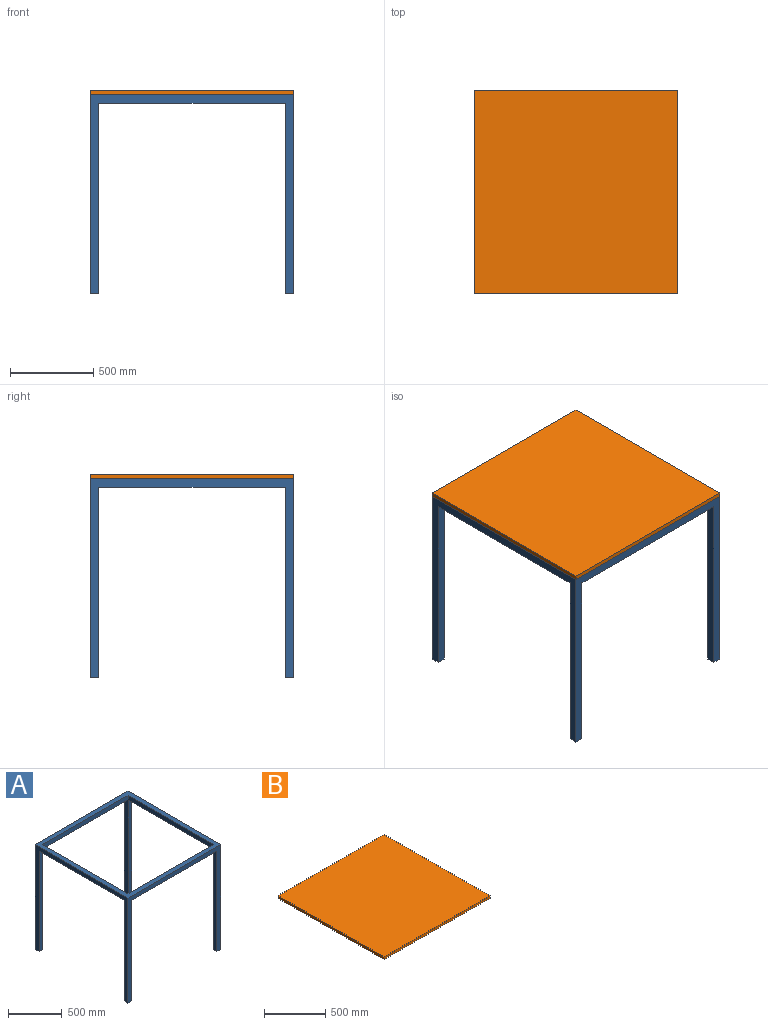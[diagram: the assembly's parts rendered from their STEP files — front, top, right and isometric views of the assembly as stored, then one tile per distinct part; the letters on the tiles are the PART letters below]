
ASSEMBLY  parts=2 mates=1
PART A: 25 faces, bbox 1219.2x1219.2x1193.8 mm
  f0: plane 1117.6x50.8mm, normal (0,0,-1), area 56774.1mm2, adj f6,f10,f20,f22
  f1: plane 1117.6x50.8mm, normal (0,0,-1), area 56774.1mm2, adj f8,f9,f17,f19
  f2: plane 1117.6x50.8mm, normal (0,0,-1), area 56774.1mm2, adj f5,f12,f14,f16
  f3: plane 1117.6x50.8mm, normal (0,0,-1), area 56774.1mm2, adj f7,f11,f13,f23
  f4: plane 1219.2x1219.2mm, normal (0,0,1), area 237418.9mm2, adj f5,f6,f7,f8,f9,f10,f11,f12
  f5: plane 1219.2x1193.8mm, normal (0,1,0), area 178064.2mm2, adj f2,f4,f7,f8,f14,f15,f16,f18
  f6: plane 1219.2x1193.8mm, normal (0,-1,0), area 178064.2mm2, adj f0,f4,f7,f8,f20,f21,f22,f24
  f7: plane 1219.2x1193.8mm, normal (1,0,0), area 178064.2mm2, adj f3,f4,f5,f6,f13,f15,f23,f24
  f8: plane 1219.2x1193.8mm, normal (-1,0,0), area 178064.2mm2, adj f1,f4,f5,f6,f17,f18,f19,f21
  f9: plane 1117.6x50.8mm, normal (1,0,0), area 56774.1mm2, adj f1,f4,f10,f12
  f10: plane 1117.6x50.8mm, normal (0,1,0), area 56774.1mm2, adj f0,f4,f9,f11
  f11: plane 1117.6x50.8mm, normal (-1,0,0), area 56774.1mm2, adj f3,f4,f10,f12
  f12: plane 1117.6x50.8mm, normal (0,-1,0), area 56774.1mm2, adj f2,f4,f9,f11
  f13: plane 1143x50.8mm, normal (0,-1,0), area 58064.4mm2, adj f3,f7,f14,f15
  f14: plane 1143x50.8mm, normal (-1,0,0), area 58064.4mm2, adj f2,f5,f13,f15
  f15: plane 50.8x50.8mm, normal (0,0,-1), area 2580.6mm2, adj f5,f7,f13,f14
  f16: plane 1143x50.8mm, normal (1,0,0), area 58064.4mm2, adj f2,f5,f17,f18
  f17: plane 1143x50.8mm, normal (0,-1,0), area 58064.4mm2, adj f1,f8,f16,f18
  f18: plane 50.8x50.8mm, normal (0,0,-1), area 2580.6mm2, adj f5,f8,f16,f17
  f19: plane 1143x50.8mm, normal (0,1,0), area 58064.4mm2, adj f1,f8,f20,f21
  f20: plane 1143x50.8mm, normal (1,0,0), area 58064.4mm2, adj f0,f6,f19,f21
  f21: plane 50.8x50.8mm, normal (0,0,-1), area 2580.6mm2, adj f6,f8,f19,f20
  f22: plane 1143x50.8mm, normal (-1,0,0), area 58064.4mm2, adj f0,f6,f23,f24
  f23: plane 1143x50.8mm, normal (0,1,0), area 58064.4mm2, adj f3,f7,f22,f24
  f24: plane 50.8x50.8mm, normal (0,0,-1), area 2580.6mm2, adj f6,f7,f22,f23
PART B: 6 faces, bbox 1219.2x1219.2x25.4 mm
  f0: plane 1219.2x25.4mm, normal (-1,0,0), area 30967.7mm2, adj f1,f3,f4,f5
  f1: plane 1219.2x25.4mm, normal (0,-1,0), area 30967.7mm2, adj f0,f2,f4,f5
  f2: plane 1219.2x25.4mm, normal (1,0,0), area 30967.7mm2, adj f1,f3,f4,f5
  f3: plane 1219.2x25.4mm, normal (0,1,0), area 30967.7mm2, adj f0,f2,f4,f5
  f4: plane 1219.2x1219.2mm, normal (0,0,1), area 1486448.6mm2, adj f0,f1,f2,f3
  f5: plane 1219.2x1219.2mm, normal (0,0,-1), area 1486448.6mm2, adj f0,f1,f2,f3
PLACE A t=(130.06,-239.24,-159.76)mm
PLACE B t=(124.41,-294.58,-135.7)mm
MATE fastened B.f5 <-> A.f4  axis (0,0,1) through (1349.26,-294.58,-135.7)mm
